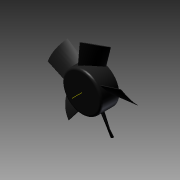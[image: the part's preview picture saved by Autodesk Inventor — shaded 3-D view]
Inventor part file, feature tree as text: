
AUTODESK INVENTOR PART (.ipt)
format: ipt  version: 2011 (Build 150239000, 239)  size: 167,424 bytes
history: native  units: mm (DEFAULTED — no unit token found)
features: sketch x6, extrude x3, plane x3, fillet x1, loft x1, other x1, pattern_circular x1
ambient origin geometry x8: Origin, YZ Plane, XZ Plane, XY Plane, X Axis, Y Axis, Z Axis, Center Point
bodies: Solid1 (feature_tree)
feature tree (16):
  extrude  "Extrusion1"  Depth=26.416mm TaperAngle=0.0deg
  fillet  "Fillet1"  Radius=3.175mm
  sketch  "Sketch2"  dims[d5=38.1mm d6=-12.7mm]
  plane  "Work Plane1"
  plane  "Work Plane2"
  sketch  "Sketch4"  dims[d7=0.0mm d8=90.0deg]
  plane  "Work Plane3"
  loft  "Loft1"
  other  "Work Axis1"
  pattern_circular  "Circular Pattern1"  Count=5 Angle=360.0deg
  extrude  "Extrusion2"  Depth=1.27mm
  extrude  "Extrusion3"  Depth=22.225mm TaperAngle=0.0deg
  sketch  "Sketch1"  dims[d0=57.785mm d1=26.416mm d2=0.0mm d3=3.175mm]
  sketch  "Sketch5"  dims[d9=0.0mm d10=90.0deg]
  sketch  "Sketch6"  dims[d11=114.3mm]
  sketch  "Sketch7"  dims[d12=26.416mm d13=0.0mm d14=50.0mm d16=360.0deg d17=1.27mm d18=22.225mm d19=0.0mm]
